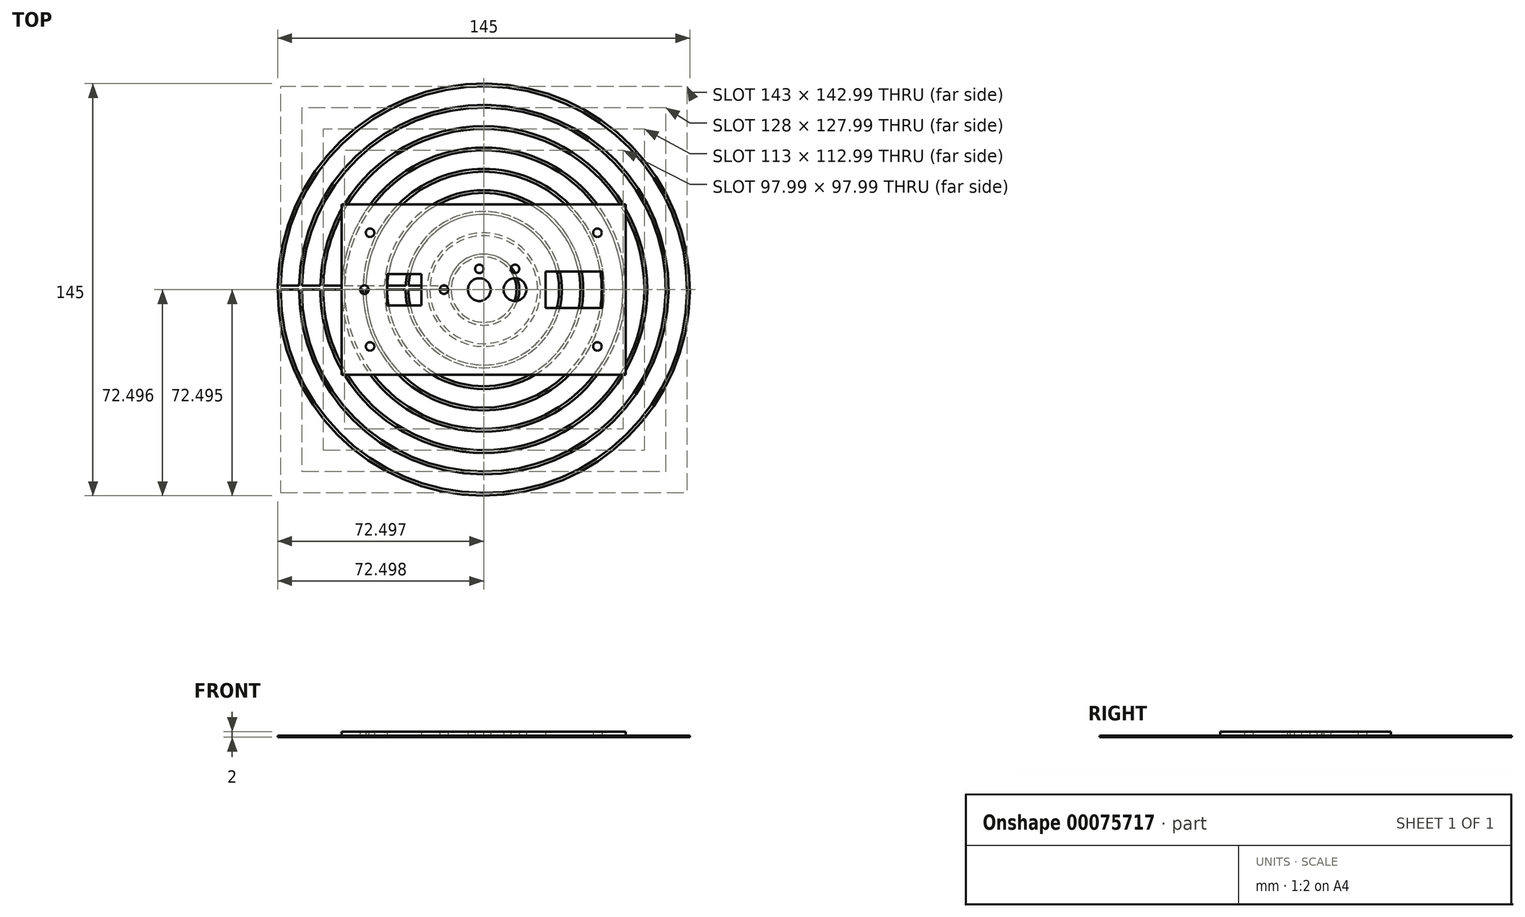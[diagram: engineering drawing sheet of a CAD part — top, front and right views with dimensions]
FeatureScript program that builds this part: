
annotation { "Feature Type Name" : "Feature", "Feature Type Description" : "" }
export const myFeature = defineFeature(function(context is Context, id is Id, definition is map)
    precondition{}
    {
        {
            var Q0;
            Q0=qCreatedBy(makeId("Top.planeOp"),FACE);
            var sketch = newSketch(context, id + "F0", { "sketchPlane" : qUnion([Q0])});
            skLineSegment(sketch, "E0.bottom", {"start": v(-50, 30) * mm, "end": v(50, 30) * mm});
            skLineSegment(sketch, "E0.top", {"start": v(-50, -30) * mm, "end": v(50, -30) * mm});
            skLineSegment(sketch, "E0.left", {"start": v(-50, 30) * mm, "end": v(-50, -30) * mm});
            skLineSegment(sketch, "E0.right", {"start": v(50, 30) * mm, "end": v(50, -30) * mm});
            skPoint(sketch, "E1", {"position": v(0, 30) * mm});
            skPoint(sketch, "E2", {"position": v(0, -30) * mm});
            skPoint(sketch, "E3", {"position": v(-50, 0) * mm});
            skPoint(sketch, "E4", {"position": v(50, 0) * mm});
            skCircle(sketch, "E5", {"center": v(-40, 20) * mm, "radius": 1.5 * mm});
            skCircle(sketch, "E6.MirrorC", {"center": v(40, 20) * mm, "radius": 1.5 * mm});
            skCircle(sketch, "E7.MirrorC", {"center": v(-40, -20) * mm, "radius": 1.5 * mm});
            skCircle(sketch, "E8.MirrorC", {"center": v(40, -20) * mm, "radius": 1.5 * mm});
            skLineSegment(sketch, "E9", {"start": v(-50, 10) * mm, "end": v(50, 10) * mm, "construction": true});
            skLineSegment(sketch, "E10.MirrorCS", {"start": v(-50, -10) * mm, "end": v(50, -10) * mm, "construction": true});
            skLineSegment(sketch, "E11.bottom", {"start": v(21.7, 6.4) * mm, "end": v(41.7, 6.4) * mm});
            skLineSegment(sketch, "E11.top", {"start": v(21.7, -6.4) * mm, "end": v(41.7, -6.4) * mm});
            skLineSegment(sketch, "E11.left", {"start": v(21.7, 6.4) * mm, "end": v(21.7, -6.4) * mm});
            skLineSegment(sketch, "E11.right", {"start": v(41.7, 6.4) * mm, "end": v(41.7, -6.4) * mm});
            skPoint(sketch, "E12", {"position": v(21.7, 0) * mm});
            skCircle(sketch, "E13", {"center": v(10.99, 0) * mm, "radius": 4 * mm});
            skCircle(sketch, "E14", {"center": v(-1.57, 0) * mm, "radius": 4 * mm});
            skLineSegment(sketch, "E15.bottom", {"start": v(-34, 5.5) * mm, "end": v(-22, 5.5) * mm});
            skLineSegment(sketch, "E15.top", {"start": v(-34, -5.5) * mm, "end": v(-22, -5.5) * mm});
            skLineSegment(sketch, "E15.left", {"start": v(-34, 5.5) * mm, "end": v(-34, -5.5) * mm});
            skLineSegment(sketch, "E15.right", {"start": v(-22, 5.5) * mm, "end": v(-22, -5.5) * mm});
            skPoint(sketch, "E16", {"position": v(-34, 0) * mm});
            skCircle(sketch, "E17", {"center": v(-42, 0) * mm, "radius": 1.5 * mm});
            skCircle(sketch, "E18", {"center": v(-14, 0) * mm, "radius": 1.5 * mm});
            skPoint(sketch, "E19", {"position": v(-28, 5.5) * mm});
            skCircle(sketch, "E20", {"center": v(-1.57, 7.3) * mm, "radius": 1.5 * mm});
            skCircle(sketch, "E21", {"center": v(10.99, 7.3) * mm, "radius": 1.5 * mm});
            skSolve(sketch);
        }
        {
            var Q0;
            Q0 = qSketchRegion(id + "F0", true);
            extrude(context, id + "F1", {"entities" : qUnion([Q0]), "depth" : 2 * mm});
        }
        {
            var Q0;
            Q0=qCreatedBy(makeId("Top.planeOp"),FACE);
            var sketch = newSketch(context, id + "F2", { "sketchPlane" : qUnion([Q0])});
            skCircle(sketch, "E22", {"center": v(0, 0) * mm, "radius": 72.5 * mm});
            skCircle(sketch, "E23", {"center": v(0, 0) * mm, "radius": 71.5 * mm});
            skCircle(sketch, "E24", {"center": v(0, 0) * mm, "radius": 65 * mm});
            skCircle(sketch, "E25", {"center": v(0, 0) * mm, "radius": 64 * mm});
            skCircle(sketch, "E26", {"center": v(0, 0) * mm, "radius": 57.5 * mm});
            skCircle(sketch, "E27", {"center": v(0, 0) * mm, "radius": 56.5 * mm});
            skCircle(sketch, "E28", {"center": v(0, 0) * mm, "radius": 50 * mm});
            skCircle(sketch, "E29", {"center": v(0, 0) * mm, "radius": 49 * mm});
            skCircle(sketch, "E30", {"center": v(0, 0) * mm, "radius": 42.5 * mm});
            skCircle(sketch, "E31", {"center": v(0, 0) * mm, "radius": 41.5 * mm});
            skCircle(sketch, "E32", {"center": v(0, 0) * mm, "radius": 35 * mm});
            skCircle(sketch, "E33", {"center": v(0, 0) * mm, "radius": 34 * mm});
            skCircle(sketch, "E34", {"center": v(0, 0) * mm, "radius": 27.5 * mm});
            skCircle(sketch, "E35", {"center": v(0, 0) * mm, "radius": 26.5 * mm});
            skCircle(sketch, "E36", {"center": v(0, 0) * mm, "radius": 20 * mm});
            skCircle(sketch, "E37", {"center": v(0, 0) * mm, "radius": 19 * mm});
            skCircle(sketch, "E38", {"center": v(0, 0) * mm, "radius": 12.5 * mm});
            skCircle(sketch, "E39", {"center": v(0, 0) * mm, "radius": 11.5 * mm});
            skLineSegment(sketch, "E40", {"start": v(-72.49, 1.47) * mm, "end": v(-11.4, 1.47) * mm});
            skLineSegment(sketch, "E41", {"start": v(-11.4, 1.47) * mm, "end": v(-11.4, 0) * mm});
            skLineSegment(sketch, "E42", {"start": v(-11.4, 0) * mm, "end": v(-72.5, 0) * mm});
            skLineSegment(sketch, "E43", {"start": v(-72.5, 0) * mm, "end": v(-72.49, 1.47) * mm});
            skSolve(sketch);
        }
        {
            var Q0;
            {var subQ1=sQuery(id+"F2.wireOp",EDGE,"E40");var subQ6=sQuery(id+"F2.wireOp",EDGE,"E23");var subQ7=makeQuery(id+"F2.imprint","INTERSECT",VERTEX,{"derivedFrom":[subQ6,subQ1]});Q0=makeQuery(id+"F2.imprint","IMPRINT",FACE,{"disambiguationData":[TD([[makeQuery(id+"F2.imprint","IMPRINT",EDGE,{"disambiguationData":[TD([[subQ7,1.0]])],"derivedFrom":subQ6}),-1.0]])]});}
            var Q1;
            {var subQ5=sQuery(id+"F2.wireOp",EDGE,"E43");Q1=makeQuery(id+"F2.imprint","IMPRINT",FACE,{"disambiguationData":[TD([[makeQuery(id+"F2.imprint","IMPRINT",EDGE,{"derivedFrom":subQ5}),-1.0]])]});}
            var Q2;
            {var subQ0=sQuery(id+"F2.wireOp",EDGE,"E40");var subQ1=sQuery(id+"F2.wireOp",EDGE,"E23");var subQ2=makeQuery(id+"F2.imprint","INTERSECT",VERTEX,{"derivedFrom":[subQ1,subQ0]});Q2=makeQuery(id+"F2.imprint","IMPRINT",FACE,{"disambiguationData":[TD([[makeQuery(id+"F2.imprint","IMPRINT",EDGE,{"disambiguationData":[TD([[subQ2,-1.0]])],"derivedFrom":subQ1}),1.0]])]});}
            var Q3;
            {var subQ0=sQuery(id+"F2.wireOp",EDGE,"E40");var subQ1=sQuery(id+"F2.wireOp",EDGE,"E24");var subQ2=makeQuery(id+"F2.imprint","INTERSECT",VERTEX,{"derivedFrom":[subQ1,subQ0]});Q3=makeQuery(id+"F2.imprint","IMPRINT",FACE,{"disambiguationData":[TD([[makeQuery(id+"F2.imprint","IMPRINT",EDGE,{"disambiguationData":[TD([[subQ2,-1.0]])],"derivedFrom":subQ1}),1.0]])]});}
            var Q4;
            {var subQ0=sQuery(id+"F2.wireOp",EDGE,"E40");var subQ1=sQuery(id+"F2.wireOp",EDGE,"E25");var subQ2=makeQuery(id+"F2.imprint","INTERSECT",VERTEX,{"derivedFrom":[subQ1,subQ0]});Q4=makeQuery(id+"F2.imprint","IMPRINT",FACE,{"disambiguationData":[TD([[makeQuery(id+"F2.imprint","IMPRINT",EDGE,{"disambiguationData":[TD([[subQ2,-1.0]])],"derivedFrom":subQ1}),1.0]])]});}
            var Q5;
            {var subQ0=sQuery(id+"F2.wireOp",EDGE,"E40");var subQ1=sQuery(id+"F2.wireOp",EDGE,"E26");var subQ2=makeQuery(id+"F2.imprint","INTERSECT",VERTEX,{"derivedFrom":[subQ1,subQ0]});Q5=makeQuery(id+"F2.imprint","IMPRINT",FACE,{"disambiguationData":[TD([[makeQuery(id+"F2.imprint","IMPRINT",EDGE,{"disambiguationData":[TD([[subQ2,-1.0]])],"derivedFrom":subQ1}),1.0]])]});}
            var Q6;
            {var subQ0=sQuery(id+"F2.wireOp",EDGE,"E40");var subQ1=sQuery(id+"F2.wireOp",EDGE,"E27");var subQ2=makeQuery(id+"F2.imprint","INTERSECT",VERTEX,{"derivedFrom":[subQ1,subQ0]});Q6=makeQuery(id+"F2.imprint","IMPRINT",FACE,{"disambiguationData":[TD([[makeQuery(id+"F2.imprint","IMPRINT",EDGE,{"disambiguationData":[TD([[subQ2,-1.0]])],"derivedFrom":subQ1}),1.0]])]});}
            var Q7;
            {var subQ0=sQuery(id+"F2.wireOp",EDGE,"E40");var subQ1=sQuery(id+"F2.wireOp",EDGE,"E28");var subQ2=makeQuery(id+"F2.imprint","INTERSECT",VERTEX,{"derivedFrom":[subQ1,subQ0]});Q7=makeQuery(id+"F2.imprint","IMPRINT",FACE,{"disambiguationData":[TD([[makeQuery(id+"F2.imprint","IMPRINT",EDGE,{"disambiguationData":[TD([[subQ2,-1.0]])],"derivedFrom":subQ1}),1.0]])]});}
            var Q8;
            {var subQ0=sQuery(id+"F2.wireOp",EDGE,"E40");var subQ1=sQuery(id+"F2.wireOp",EDGE,"E29");var subQ2=makeQuery(id+"F2.imprint","INTERSECT",VERTEX,{"derivedFrom":[subQ1,subQ0]});Q8=makeQuery(id+"F2.imprint","IMPRINT",FACE,{"disambiguationData":[TD([[makeQuery(id+"F2.imprint","IMPRINT",EDGE,{"disambiguationData":[TD([[subQ2,-1.0]])],"derivedFrom":subQ1}),1.0]])]});}
            var Q9;
            {var subQ0=sQuery(id+"F2.wireOp",EDGE,"E40");var subQ1=sQuery(id+"F2.wireOp",EDGE,"E30");var subQ2=makeQuery(id+"F2.imprint","INTERSECT",VERTEX,{"derivedFrom":[subQ1,subQ0]});Q9=makeQuery(id+"F2.imprint","IMPRINT",FACE,{"disambiguationData":[TD([[makeQuery(id+"F2.imprint","IMPRINT",EDGE,{"disambiguationData":[TD([[subQ2,-1.0]])],"derivedFrom":subQ1}),1.0]])]});}
            var Q10;
            {var subQ0=sQuery(id+"F2.wireOp",EDGE,"E40");var subQ1=sQuery(id+"F2.wireOp",EDGE,"E31");var subQ2=makeQuery(id+"F2.imprint","INTERSECT",VERTEX,{"derivedFrom":[subQ1,subQ0]});Q10=makeQuery(id+"F2.imprint","IMPRINT",FACE,{"disambiguationData":[TD([[makeQuery(id+"F2.imprint","IMPRINT",EDGE,{"disambiguationData":[TD([[subQ2,-1.0]])],"derivedFrom":subQ1}),1.0]])]});}
            var Q11;
            {var subQ0=sQuery(id+"F2.wireOp",EDGE,"E40");var subQ1=sQuery(id+"F2.wireOp",EDGE,"E32");var subQ2=makeQuery(id+"F2.imprint","INTERSECT",VERTEX,{"derivedFrom":[subQ1,subQ0]});Q11=makeQuery(id+"F2.imprint","IMPRINT",FACE,{"disambiguationData":[TD([[makeQuery(id+"F2.imprint","IMPRINT",EDGE,{"disambiguationData":[TD([[subQ2,-1.0]])],"derivedFrom":subQ1}),1.0]])]});}
            var Q12;
            {var subQ0=sQuery(id+"F2.wireOp",EDGE,"E40");var subQ1=sQuery(id+"F2.wireOp",EDGE,"E33");var subQ2=makeQuery(id+"F2.imprint","INTERSECT",VERTEX,{"derivedFrom":[subQ1,subQ0]});Q12=makeQuery(id+"F2.imprint","IMPRINT",FACE,{"disambiguationData":[TD([[makeQuery(id+"F2.imprint","IMPRINT",EDGE,{"disambiguationData":[TD([[subQ2,-1.0]])],"derivedFrom":subQ1}),1.0]])]});}
            var Q13;
            {var subQ0=sQuery(id+"F2.wireOp",EDGE,"E40");var subQ1=sQuery(id+"F2.wireOp",EDGE,"E34");var subQ2=makeQuery(id+"F2.imprint","INTERSECT",VERTEX,{"derivedFrom":[subQ1,subQ0]});Q13=makeQuery(id+"F2.imprint","IMPRINT",FACE,{"disambiguationData":[TD([[makeQuery(id+"F2.imprint","IMPRINT",EDGE,{"disambiguationData":[TD([[subQ2,-1.0]])],"derivedFrom":subQ1}),1.0]])]});}
            var Q14;
            {var subQ0=sQuery(id+"F2.wireOp",EDGE,"E40");var subQ1=sQuery(id+"F2.wireOp",EDGE,"E35");var subQ2=makeQuery(id+"F2.imprint","INTERSECT",VERTEX,{"derivedFrom":[subQ1,subQ0]});Q14=makeQuery(id+"F2.imprint","IMPRINT",FACE,{"disambiguationData":[TD([[makeQuery(id+"F2.imprint","IMPRINT",EDGE,{"disambiguationData":[TD([[subQ2,-1.0]])],"derivedFrom":subQ1}),1.0]])]});}
            var Q15;
            {var subQ0=sQuery(id+"F2.wireOp",EDGE,"E40");var subQ1=sQuery(id+"F2.wireOp",EDGE,"E36");var subQ2=makeQuery(id+"F2.imprint","INTERSECT",VERTEX,{"derivedFrom":[subQ1,subQ0]});Q15=makeQuery(id+"F2.imprint","IMPRINT",FACE,{"disambiguationData":[TD([[makeQuery(id+"F2.imprint","IMPRINT",EDGE,{"disambiguationData":[TD([[subQ2,-1.0]])],"derivedFrom":subQ1}),1.0]])]});}
            var Q16;
            {var subQ0=sQuery(id+"F2.wireOp",EDGE,"E40");var subQ1=sQuery(id+"F2.wireOp",EDGE,"E38");var subQ2=makeQuery(id+"F2.imprint","INTERSECT",VERTEX,{"derivedFrom":[subQ1,subQ0]});Q16=makeQuery(id+"F2.imprint","IMPRINT",FACE,{"disambiguationData":[TD([[makeQuery(id+"F2.imprint","IMPRINT",EDGE,{"disambiguationData":[TD([[subQ2,-1.0]])],"derivedFrom":subQ1}),1.0]])]});}
            var Q17;
            {var subQ0=sQuery(id+"F2.wireOp",EDGE,"E40");var subQ1=sQuery(id+"F2.wireOp",EDGE,"E38");var subQ2=makeQuery(id+"F2.imprint","INTERSECT",VERTEX,{"derivedFrom":[subQ1,subQ0]});Q17=makeQuery(id+"F2.imprint","IMPRINT",FACE,{"disambiguationData":[TD([[makeQuery(id+"F2.imprint","IMPRINT",EDGE,{"disambiguationData":[TD([[subQ2,1.0]])],"derivedFrom":subQ1}),1.0]])]});}
            var Q18;
            {var subQ0=sQuery(id+"F2.wireOp",EDGE,"E40");var subQ1=sQuery(id+"F2.wireOp",EDGE,"E36");var subQ2=makeQuery(id+"F2.imprint","INTERSECT",VERTEX,{"derivedFrom":[subQ1,subQ0]});Q18=makeQuery(id+"F2.imprint","IMPRINT",FACE,{"disambiguationData":[TD([[makeQuery(id+"F2.imprint","IMPRINT",EDGE,{"disambiguationData":[TD([[subQ2,1.0]])],"derivedFrom":subQ1}),1.0]])]});}
            var Q19;
            {var subQ0=sQuery(id+"F2.wireOp",EDGE,"E40");var subQ1=sQuery(id+"F2.wireOp",EDGE,"E34");var subQ2=makeQuery(id+"F2.imprint","INTERSECT",VERTEX,{"derivedFrom":[subQ1,subQ0]});Q19=makeQuery(id+"F2.imprint","IMPRINT",FACE,{"disambiguationData":[TD([[makeQuery(id+"F2.imprint","IMPRINT",EDGE,{"disambiguationData":[TD([[subQ2,1.0]])],"derivedFrom":subQ1}),1.0]])]});}
            var Q20;
            {var subQ0=sQuery(id+"F2.wireOp",EDGE,"E40");var subQ1=sQuery(id+"F2.wireOp",EDGE,"E32");var subQ2=makeQuery(id+"F2.imprint","INTERSECT",VERTEX,{"derivedFrom":[subQ1,subQ0]});Q20=makeQuery(id+"F2.imprint","IMPRINT",FACE,{"disambiguationData":[TD([[makeQuery(id+"F2.imprint","IMPRINT",EDGE,{"disambiguationData":[TD([[subQ2,1.0]])],"derivedFrom":subQ1}),1.0]])]});}
            var Q21;
            {var subQ0=sQuery(id+"F2.wireOp",EDGE,"E40");var subQ1=sQuery(id+"F2.wireOp",EDGE,"E30");var subQ2=makeQuery(id+"F2.imprint","INTERSECT",VERTEX,{"derivedFrom":[subQ1,subQ0]});Q21=makeQuery(id+"F2.imprint","IMPRINT",FACE,{"disambiguationData":[TD([[makeQuery(id+"F2.imprint","IMPRINT",EDGE,{"disambiguationData":[TD([[subQ2,1.0]])],"derivedFrom":subQ1}),1.0]])]});}
            var Q22;
            {var subQ0=sQuery(id+"F2.wireOp",EDGE,"E40");var subQ1=sQuery(id+"F2.wireOp",EDGE,"E28");var subQ2=makeQuery(id+"F2.imprint","INTERSECT",VERTEX,{"derivedFrom":[subQ1,subQ0]});Q22=makeQuery(id+"F2.imprint","IMPRINT",FACE,{"disambiguationData":[TD([[makeQuery(id+"F2.imprint","IMPRINT",EDGE,{"disambiguationData":[TD([[subQ2,1.0]])],"derivedFrom":subQ1}),1.0]])]});}
            var Q23;
            {var subQ0=sQuery(id+"F2.wireOp",EDGE,"E40");var subQ1=sQuery(id+"F2.wireOp",EDGE,"E37");var subQ2=makeQuery(id+"F2.imprint","INTERSECT",VERTEX,{"derivedFrom":[subQ1,subQ0]});Q23=makeQuery(id+"F2.imprint","IMPRINT",FACE,{"disambiguationData":[TD([[makeQuery(id+"F2.imprint","IMPRINT",EDGE,{"disambiguationData":[TD([[subQ2,-1.0]])],"derivedFrom":subQ1}),1.0]])]});}
            var Q24;
            {var subQ0=sQuery(id+"F2.wireOp",EDGE,"E40");var subQ1=sQuery(id+"F2.wireOp",EDGE,"E26");var subQ2=makeQuery(id+"F2.imprint","INTERSECT",VERTEX,{"derivedFrom":[subQ1,subQ0]});Q24=makeQuery(id+"F2.imprint","IMPRINT",FACE,{"disambiguationData":[TD([[makeQuery(id+"F2.imprint","IMPRINT",EDGE,{"disambiguationData":[TD([[subQ2,1.0]])],"derivedFrom":subQ1}),1.0]])]});}
            var Q25;
            {var subQ0=sQuery(id+"F2.wireOp",EDGE,"E40");var subQ1=sQuery(id+"F2.wireOp",EDGE,"E24");var subQ2=makeQuery(id+"F2.imprint","INTERSECT",VERTEX,{"derivedFrom":[subQ1,subQ0]});Q25=makeQuery(id+"F2.imprint","IMPRINT",FACE,{"disambiguationData":[TD([[makeQuery(id+"F2.imprint","IMPRINT",EDGE,{"disambiguationData":[TD([[subQ2,1.0]])],"derivedFrom":subQ1}),1.0]])]});}
            extrude(context, id + "F3", {"entities" : qUnion([Q0, Q1, Q2, Q3, Q4, Q5, Q6, Q7, Q8, Q9, Q10, Q11, Q12, Q13, Q14, Q15, Q16, Q17, Q18, Q19, Q20, Q21, Q22, Q23, Q24, Q25]), "depth" : 0.5 * mm});
        }
    });
